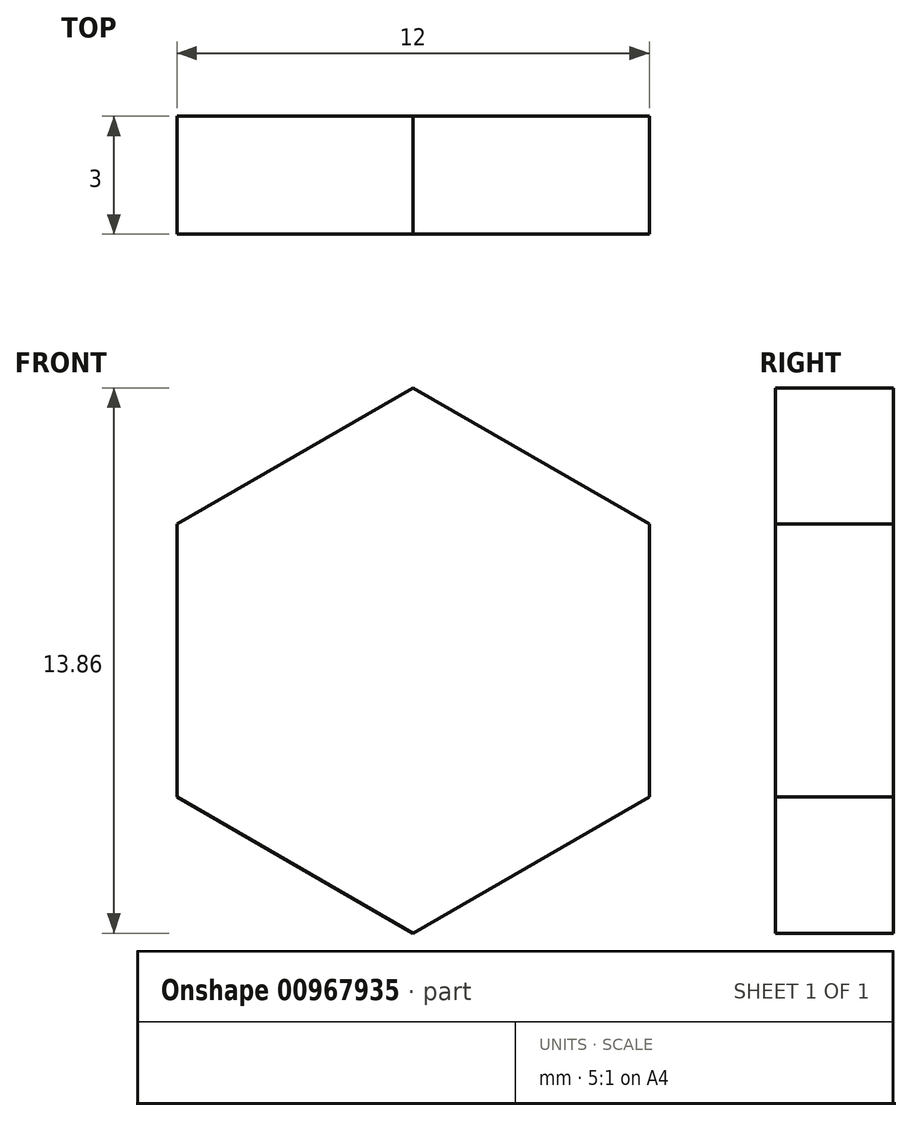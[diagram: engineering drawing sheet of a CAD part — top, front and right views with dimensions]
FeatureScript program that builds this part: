
annotation { "Feature Type Name" : "Feature", "Feature Type Description" : "" }
export const myFeature = defineFeature(function(context is Context, id is Id, definition is map)
    precondition{}
    {
        {
            var Q0;
            Q0=qCreatedBy(makeId("Front.planeOp"),FACE);
            var sketch = newSketch(context, id + "F0", { "sketchPlane" : qUnion([Q0])});
            skLineSegment(sketch, "E0", {"start": v(0, 6.93) * mm, "end": v(0, -6.93) * mm});
            skLineSegment(sketch, "E1", {"start": v(-6, 3.46) * mm, "end": v(6, -3.46) * mm});
            skLineSegment(sketch, "E2", {"start": v(0, 6.93) * mm, "end": v(-6, 3.46) * mm});
            skLineSegment(sketch, "E3", {"start": v(-6, 3.46) * mm, "end": v(-6, -3.46) * mm});
            skLineSegment(sketch, "E4", {"start": v(-6, -3.46) * mm, "end": v(0, -6.93) * mm});
            skLineSegment(sketch, "E5", {"start": v(6, -3.46) * mm, "end": v(0, -6.93) * mm});
            skLineSegment(sketch, "E6", {"start": v(6, 3.46) * mm, "end": v(6, -3.46) * mm});
            skLineSegment(sketch, "E7", {"start": v(-6, -3.46) * mm, "end": v(6, 3.46) * mm});
            skLineSegment(sketch, "E8", {"start": v(0, 6.93) * mm, "end": v(6, 3.46) * mm});
            skSolve(sketch);
        }
        {
            var Q0;
            Q0 = qSketchRegion(id + "F0", true);
            extrude(context, id + "F1", {"entities" : qUnion([Q0]), "depth" : 3 * mm, "offsetDistance" : 25 * mm, "symmetric" : true});
        }
    });
